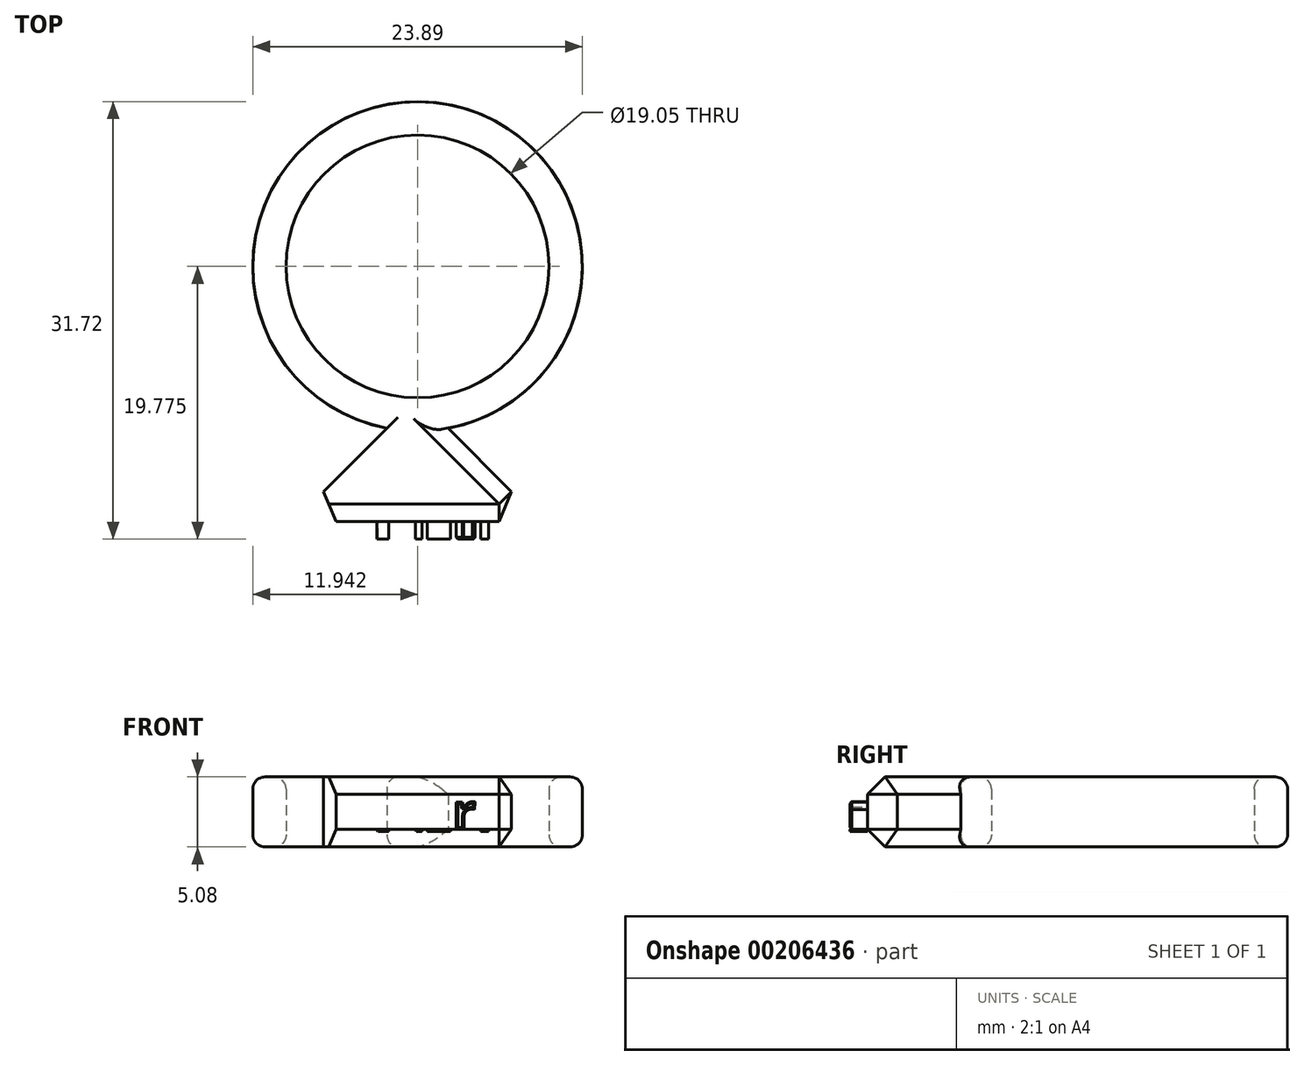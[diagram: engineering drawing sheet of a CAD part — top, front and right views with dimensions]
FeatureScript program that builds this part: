
annotation { "Feature Type Name" : "Feature", "Feature Type Description" : "" }
export const myFeature = defineFeature(function(context is Context, id is Id, definition is map)
    precondition{}
    {
        {
            var Q0;
            Q0=qCreatedBy(makeId("Top.planeOp"),FACE);
            var sketch = newSketch(context, id + "F0", { "sketchPlane" : qUnion([Q0])});
            skCircle(sketch, "E0", {"center": v(-464.76, 144.02) * mm, "radius": 9.53 * mm});
            skCircle(sketch, "E1", {"center": v(-464.76, 144.02) * mm, "radius": 11.95 * mm});
            skLineSegment(sketch, "E2", {"start": v(-464.76, 134.5) * mm, "end": v(-473.74, 125.52) * mm});
            skLineSegment(sketch, "E3", {"start": v(-473.74, 125.52) * mm, "end": v(-464.76, 134.5) * mm});
            skLineSegment(sketch, "E4", {"start": v(-464.76, 134.5) * mm, "end": v(-455.78, 125.52) * mm});
            skLineSegment(sketch, "E5", {"start": v(-473.74, 125.52) * mm, "end": v(-455.78, 125.52) * mm});
            skSolve(sketch);
        }
        {
            var Q0;
            {var subQ5=sQuery(id+"F0.wireOp",EDGE,"E5");Q0=makeQuery(id+"F0.imprint","IMPRINT",FACE,{"disambiguationData":[TD([[makeQuery(id+"F0.imprint","IMPRINT",EDGE,{"derivedFrom":subQ5}),1.0]])]});}
            var Q1;
            {var subQ0=sQuery(id+"F0.wireOp",EDGE,"E3");var subQ1=sQuery(id+"F0.wireOp",EDGE,"E1");var subQ2=makeQuery(id+"F0.imprint","INTERSECT",VERTEX,{"derivedFrom":[subQ1,subQ0]});Q1=makeQuery(id+"F0.imprint","IMPRINT",FACE,{"disambiguationData":[TD([[makeQuery(id+"F0.imprint","IMPRINT",EDGE,{"disambiguationData":[TD([[subQ2,-1.0]])],"derivedFrom":subQ1}),1.0]])]});}
            var Q2;
            {var subQ0=sQuery(id+"F0.wireOp",EDGE,"E0");Q2=makeQuery(id+"F0.imprint","IMPRINT",FACE,{"disambiguationData":[TD([[makeQuery(id+"F0.imprint","IMPRINT",EDGE,{"derivedFrom":subQ0}),-1.0]])]});}
            extrude(context, id + "F1", {"entities" : qUnion([Q0, Q1, Q2]), "depth" : 5.08 * mm});
        }
        {
            var Q0;
            Q0=makeQuery(id+"F1.opExtrude","SWEPT_EDGE",EDGE,{"disambiguationData":[OSD([sQuery(id+"F0.wireOp",EDGE,"E4"),sQuery(id+"F0.wireOp",EDGE,"E5")])]});
            var Q1;
            Q1=makeQuery(id+"F1.opExtrude","CAP_EDGE",EDGE,{"disambiguationData":[OSD([sQuery(id+"F0.wireOp",EDGE,"E5")])],"isStart":true});
            var Q2;
            Q2=makeQuery(id+"F1.opExtrude","SWEPT_EDGE",EDGE,{"disambiguationData":[OSD([sQuery(id+"F0.wireOp",EDGE,"E3"),sQuery(id+"F0.wireOp",EDGE,"E5")])]});
            var Q3;
            Q3=makeQuery(id+"F1.opExtrude","CAP_EDGE",EDGE,{"disambiguationData":[OSD([sQuery(id+"F0.wireOp",EDGE,"E5")])],"isStart":false});
            var Q4;
            Q4=makeQuery(id+"F1.opExtrude","CAP_EDGE",EDGE,{"disambiguationData":[OSD([sQuery(id+"F0.wireOp",EDGE,"E4")])],"isStart":false});
            var Q5;
            Q5=makeQuery(id+"F1.opExtrude","CAP_EDGE",EDGE,{"disambiguationData":[OSD([sQuery(id+"F0.wireOp",EDGE,"E3")])],"isStart":false});
            var Q6;
            Q6=makeQuery(id+"F1.opExtrude","CAP_EDGE",EDGE,{"disambiguationData":[OSD([sQuery(id+"F0.wireOp",EDGE,"E4")])],"isStart":true});
            var Q7;
            Q7=makeQuery(id+"F1.opExtrude","CAP_EDGE",EDGE,{"disambiguationData":[OSD([sQuery(id+"F0.wireOp",EDGE,"E3")])],"isStart":true});
            chamfer(context, id + "F2", {"entities" : qUnion([Q0, Q1, Q2, Q3, Q4, Q5, Q6, Q7]), "width" : 1.27 * mm, "tangentPropagation" : true});
        }
        {
            var Q0;
            Q0=makeQuery(id+"F1.opExtrude","SWEPT_FACE",FACE,{"disambiguationData":[OSD([sQuery(id+"F0.wireOp",EDGE,"E5")])]});
            var sketch = newSketch(context, id + "F3", { "sketchPlane" : qUnion([Q0])});
            skText(sketch, "E6", { "text": "Nazri", "fontName": "OpenSans-Bold.ttf"});
            const initialGuessF3  = {"E6": [-0.46967, 0.00112, 1, 0, 0.0028]};
            skSetInitialGuess(sketch, initialGuessF3);
            skSolve(sketch);
        }
        {
            var Q0;
            Q0=makeQuery(id+"F3.imprint","IMPRINT",FACE,{"disambiguationData":[TD([[makeQuery(id+"F3.imprint","IMPRINT",EDGE,{"derivedFrom":sQuery(id+"F3.wireOp",EDGE,"E6.sketch_text.stroke-0")}),-1.0]])]});
            var Q1;
            Q1=makeQuery(id+"F3.imprint","IMPRINT",FACE,{"disambiguationData":[TD([[makeQuery(id+"F3.imprint","IMPRINT",EDGE,{"derivedFrom":sQuery(id+"F3.wireOp",EDGE,"E6.sketch_text.stroke-14")}),-1.0]])]});
            var Q2;
            Q2=makeQuery(id+"F3.imprint","IMPRINT",FACE,{"disambiguationData":[TD([[makeQuery(id+"F3.imprint","IMPRINT",EDGE,{"derivedFrom":sQuery(id+"F3.wireOp",EDGE,"E6.sketch_text.stroke-39")}),-1.0]])]});
            var Q3;
            Q3=makeQuery(id+"F3.imprint","IMPRINT",FACE,{"disambiguationData":[TD([[makeQuery(id+"F3.imprint","IMPRINT",EDGE,{"derivedFrom":sQuery(id+"F3.wireOp",EDGE,"E6.sketch_text.stroke-49")}),-1.0]])]});
            var Q4;
            Q4=makeQuery(id+"F3.imprint","IMPRINT",FACE,{"disambiguationData":[TD([[makeQuery(id+"F3.imprint","IMPRINT",EDGE,{"derivedFrom":sQuery(id+"F3.wireOp",EDGE,"E6.sketch_text.stroke-67")}),-1.0]])]});
            extrude(context, id + "F4", {"entities" : qUnion([Q0, Q1, Q2, Q3, Q4]), "operationType" : NewBodyOperationType.ADD, "depth" : 1.27 * mm});
        }
        {
            var Q0;
            Q0=makeQuery(id+"F4.opExtrude","CAP_EDGE",EDGE,{"disambiguationData":[OSD([sQuery(id+"F3.wireOp",EDGE,"E6.sketch_text.stroke-6")])],"isStart":false});
            var Q1;
            Q1=makeQuery(id+"F4.opExtrude","CAP_EDGE",EDGE,{"disambiguationData":[OSD([sQuery(id+"F3.wireOp",EDGE,"E6.sketch_text.stroke-5")])],"isStart":false});
            var Q2;
            Q2=makeQuery(id+"F4.opExtrude","CAP_EDGE",EDGE,{"disambiguationData":[OSD([sQuery(id+"F3.wireOp",EDGE,"E6.sketch_text.stroke-4")])],"isStart":false});
            var Q3;
            Q3=makeQuery(id+"F4.opExtrude","CAP_EDGE",EDGE,{"disambiguationData":[OSD([sQuery(id+"F3.wireOp",EDGE,"E6.sketch_text.stroke-7")])],"isStart":false});
            var Q4;
            Q4=makeQuery(id+"F4.opExtrude","CAP_EDGE",EDGE,{"disambiguationData":[OSD([sQuery(id+"F3.wireOp",EDGE,"E6.sketch_text.stroke-1")])],"isStart":false});
            var Q5;
            Q5=makeQuery(id+"F4.opExtrude","CAP_FACE",FACE,{"disambiguationData":[OSD([sQuery(id+"F3.wireOp",EDGE,"E6.sketch_text.stroke-0"),sQuery(id+"F3.wireOp",EDGE,"E6.sketch_text.stroke-1"),sQuery(id+"F3.wireOp",EDGE,"E6.sketch_text.stroke-2"),sQuery(id+"F3.wireOp",EDGE,"E6.sketch_text.stroke-3"),sQuery(id+"F3.wireOp",EDGE,"E6.sketch_text.stroke-4"),sQuery(id+"F3.wireOp",EDGE,"E6.sketch_text.stroke-5"),sQuery(id+"F3.wireOp",EDGE,"E6.sketch_text.stroke-6"),sQuery(id+"F3.wireOp",EDGE,"E6.sketch_text.stroke-7"),sQuery(id+"F3.wireOp",EDGE,"E6.sketch_text.stroke-8"),sQuery(id+"F3.wireOp",EDGE,"E6.sketch_text.stroke-9"),sQuery(id+"F3.wireOp",EDGE,"E6.sketch_text.stroke-10"),sQuery(id+"F3.wireOp",EDGE,"E6.sketch_text.stroke-11"),sQuery(id+"F3.wireOp",EDGE,"E6.sketch_text.stroke-12"),sQuery(id+"F3.wireOp",EDGE,"E6.sketch_text.stroke-13")])],"isStart":false});
            var Q6;
            Q6=makeQuery(id+"F4.opExtrude","CAP_FACE",FACE,{"disambiguationData":[OSD([sQuery(id+"F3.wireOp",EDGE,"E6.sketch_text.stroke-14"),sQuery(id+"F3.wireOp",EDGE,"E6.sketch_text.stroke-15"),sQuery(id+"F3.wireOp",EDGE,"E6.sketch_text.stroke-16"),sQuery(id+"F3.wireOp",EDGE,"E6.sketch_text.stroke-17"),sQuery(id+"F3.wireOp",EDGE,"E6.sketch_text.stroke-18"),sQuery(id+"F3.wireOp",EDGE,"E6.sketch_text.stroke-19"),sQuery(id+"F3.wireOp",EDGE,"E6.sketch_text.stroke-20"),sQuery(id+"F3.wireOp",EDGE,"E6.sketch_text.stroke-21"),sQuery(id+"F3.wireOp",EDGE,"E6.sketch_text.stroke-22"),sQuery(id+"F3.wireOp",EDGE,"E6.sketch_text.stroke-23"),sQuery(id+"F3.wireOp",EDGE,"E6.sketch_text.stroke-24"),sQuery(id+"F3.wireOp",EDGE,"E6.sketch_text.stroke-25"),sQuery(id+"F3.wireOp",EDGE,"E6.sketch_text.stroke-26"),sQuery(id+"F3.wireOp",EDGE,"E6.sketch_text.stroke-27"),sQuery(id+"F3.wireOp",EDGE,"E6.sketch_text.stroke-28"),sQuery(id+"F3.wireOp",EDGE,"E6.sketch_text.stroke-29"),sQuery(id+"F3.wireOp",EDGE,"E6.sketch_text.stroke-30"),sQuery(id+"F3.wireOp",EDGE,"E6.sketch_text.stroke-31"),sQuery(id+"F3.wireOp",EDGE,"E6.sketch_text.stroke-32"),sQuery(id+"F3.wireOp",EDGE,"E6.sketch_text.stroke-33"),sQuery(id+"F3.wireOp",EDGE,"E6.sketch_text.stroke-34"),sQuery(id+"F3.wireOp",EDGE,"E6.sketch_text.stroke-35"),sQuery(id+"F3.wireOp",EDGE,"E6.sketch_text.stroke-36"),sQuery(id+"F3.wireOp",EDGE,"E6.sketch_text.stroke-37"),sQuery(id+"F3.wireOp",EDGE,"E6.sketch_text.stroke-38")])],"isStart":false});
            var Q7;
            Q7=makeQuery(id+"F4.opExtrude","CAP_FACE",FACE,{"disambiguationData":[OSD([sQuery(id+"F3.wireOp",EDGE,"E6.sketch_text.stroke-39"),sQuery(id+"F3.wireOp",EDGE,"E6.sketch_text.stroke-40"),sQuery(id+"F3.wireOp",EDGE,"E6.sketch_text.stroke-41"),sQuery(id+"F3.wireOp",EDGE,"E6.sketch_text.stroke-42"),sQuery(id+"F3.wireOp",EDGE,"E6.sketch_text.stroke-43"),sQuery(id+"F3.wireOp",EDGE,"E6.sketch_text.stroke-44"),sQuery(id+"F3.wireOp",EDGE,"E6.sketch_text.stroke-45"),sQuery(id+"F3.wireOp",EDGE,"E6.sketch_text.stroke-46"),sQuery(id+"F3.wireOp",EDGE,"E6.sketch_text.stroke-47"),sQuery(id+"F3.wireOp",EDGE,"E6.sketch_text.stroke-48")])],"isStart":false});
            var Q8;
            Q8=makeQuery(id+"F4.opExtrude","CAP_FACE",FACE,{"disambiguationData":[OSD([sQuery(id+"F3.wireOp",EDGE,"E6.sketch_text.stroke-49"),sQuery(id+"F3.wireOp",EDGE,"E6.sketch_text.stroke-50"),sQuery(id+"F3.wireOp",EDGE,"E6.sketch_text.stroke-51"),sQuery(id+"F3.wireOp",EDGE,"E6.sketch_text.stroke-52"),sQuery(id+"F3.wireOp",EDGE,"E6.sketch_text.stroke-53"),sQuery(id+"F3.wireOp",EDGE,"E6.sketch_text.stroke-54"),sQuery(id+"F3.wireOp",EDGE,"E6.sketch_text.stroke-55"),sQuery(id+"F3.wireOp",EDGE,"E6.sketch_text.stroke-56"),sQuery(id+"F3.wireOp",EDGE,"E6.sketch_text.stroke-57"),sQuery(id+"F3.wireOp",EDGE,"E6.sketch_text.stroke-58"),sQuery(id+"F3.wireOp",EDGE,"E6.sketch_text.stroke-59"),sQuery(id+"F3.wireOp",EDGE,"E6.sketch_text.stroke-60"),sQuery(id+"F3.wireOp",EDGE,"E6.sketch_text.stroke-61")])],"isStart":false});
            var Q9;
            Q9=makeQuery(id+"F4.opExtrude","CAP_FACE",FACE,{"disambiguationData":[OSD([sQuery(id+"F3.wireOp",EDGE,"E6.sketch_text.stroke-67"),sQuery(id+"F3.wireOp",EDGE,"E6.sketch_text.stroke-68"),sQuery(id+"F3.wireOp",EDGE,"E6.sketch_text.stroke-69"),sQuery(id+"F3.wireOp",EDGE,"E6.sketch_text.stroke-70")])],"isStart":false});
            chamfer(context, id + "F5", {"entities" : qUnion([Q0, Q1, Q2, Q3, Q4, Q5, Q6, Q7, Q8, Q9]), "width" : 0.13 * mm, "tangentPropagation" : true});
        }
        {
            var Q0;
            Q0=makeQuery(id+"F1.opExtrude","CAP_EDGE",EDGE,{"disambiguationData":[OSD([sQuery(id+"F0.wireOp",EDGE,"E1")])],"isStart":true});
            var Q1;
            Q1=makeQuery(id+"F1.opExtrude","CAP_EDGE",EDGE,{"disambiguationData":[OSD([sQuery(id+"F0.wireOp",EDGE,"E1")])],"isStart":false});
            var Q2;
            Q2=makeQuery(id+"F1.opExtrude","CAP_EDGE",EDGE,{"disambiguationData":[OSD([sQuery(id+"F0.wireOp",EDGE,"E0")])],"isStart":true});
            var Q3;
            Q3=makeQuery(id+"F1.opExtrude","CAP_EDGE",EDGE,{"disambiguationData":[OSD([sQuery(id+"F0.wireOp",EDGE,"E0")])],"isStart":false});
            fillet(context, id + "F6", {"entities" : qUnion([Q0, Q1, Q2, Q3]), "radius" : 0.89 * mm, "tangentPropagation" : true, "allowEdgeOverflow" : false});
        }
    });
